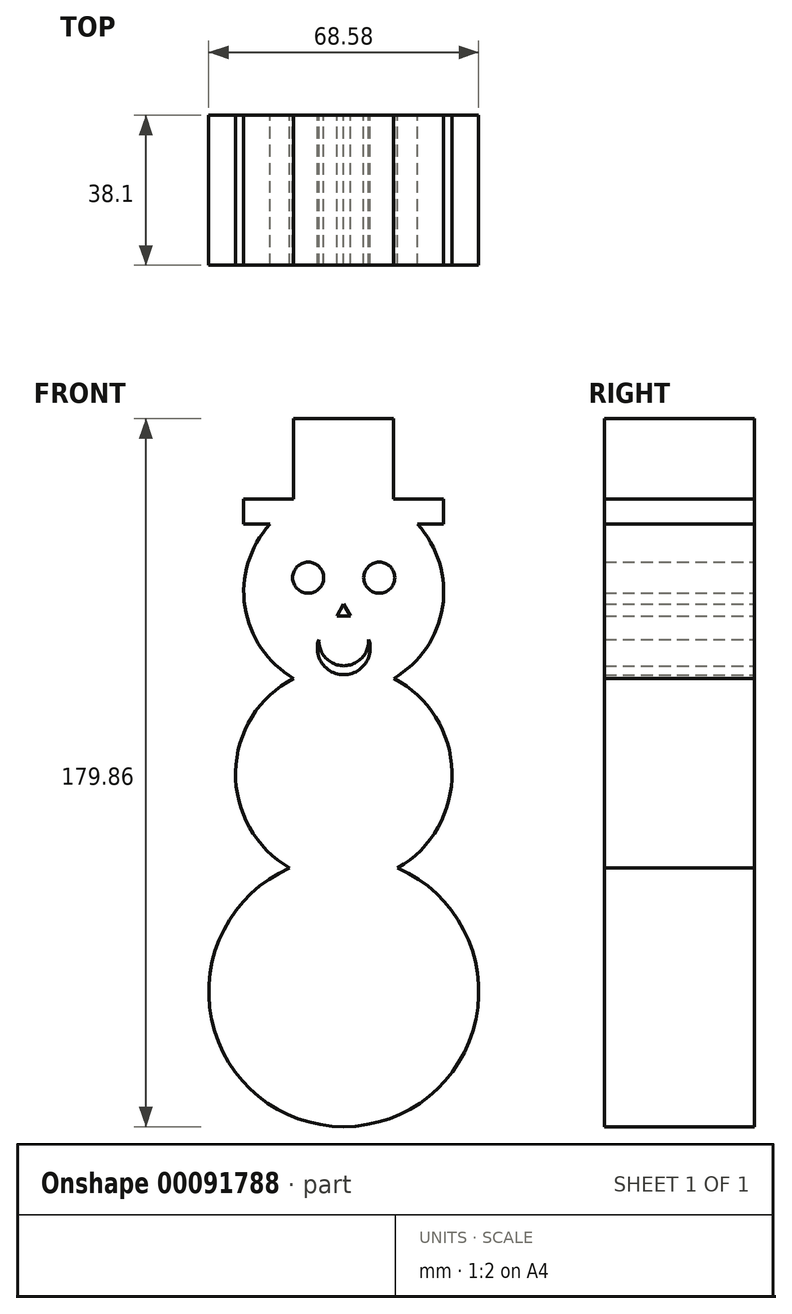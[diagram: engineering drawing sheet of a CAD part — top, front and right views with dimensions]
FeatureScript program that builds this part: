
annotation { "Feature Type Name" : "Feature", "Feature Type Description" : "" }
export const myFeature = defineFeature(function(context is Context, id is Id, definition is map)
    precondition{}
    {
        {
            var Q0;
            Q0=qCreatedBy(makeId("Front.planeOp"),FACE);
            var sketch = newSketch(context, id + "F0", { "sketchPlane" : qUnion([Q0])});
            skCircle(sketch, "E0", {"center": v(0, 0) * mm, "radius": 27.5 * mm});
            skCircle(sketch, "E1", {"center": v(0, 46.37) * mm, "radius": 25.4 * mm});
            skCircle(sketch, "E2", {"center": v(0, -55.26) * mm, "radius": 34.3 * mm});
            skCircle(sketch, "E3", {"center": v(-9.03, 49.92) * mm, "radius": 3.95 * mm});
            skCircle(sketch, "E4.MirrorC", {"center": v(9.03, 49.92) * mm, "radius": 3.95 * mm});
            skLineSegment(sketch, "E5", {"start": v(0, 43.2) * mm, "end": v(-1.7, 40.25) * mm});
            skLineSegment(sketch, "E6", {"start": v(-1.7, 40.25) * mm, "end": v(1.7, 40.25) * mm});
            skPoint(sketch, "E7.endSnap0", {"position": v(-0.85, 41.73) * mm});
            skLineSegment(sketch, "E8", {"start": v(0, 43.2) * mm, "end": v(1.7, 40.25) * mm});
            skArc(sketch, "E9", {"start": v(-6.34, 34.24) * mm, "mid": v(-4.6, 29.53) * mm, "end": v(0, 27.55) * mm});
            skArc(sketch, "E10", {"start": v(-6.34, 34.24) * mm, "mid": v(-5.5, 28.11) * mm, "end": v(0, 25.27) * mm});
            skArc(sketch, "E11.MirrorCS", {"start": v(6.34, 34.24) * mm, "mid": v(4.6, 29.53) * mm, "end": v(0, 27.55) * mm});
            skArc(sketch, "E12.MirrorCS", {"start": v(6.34, 34.24) * mm, "mid": v(5.5, 28.11) * mm, "end": v(0, 25.27) * mm});
            skSolve(sketch);
        }
        {
            var Q0;
            Q0 = qSketchRegion(id + "F0", true);
            extrude(context, id + "F1", {"entities" : qUnion([Q0]), "depth" : 38.1 * mm});
        }
        {
            var Q0;
            Q0=qCreatedBy(makeId("Front.planeOp"),FACE);
            var sketch = newSketch(context, id + "F2", { "sketchPlane" : qUnion([Q0])});
            skLineSegment(sketch, "E13.bottom", {"start": v(0, 69.85) * mm, "end": v(25.4, 69.85) * mm});
            skLineSegment(sketch, "E13.top", {"start": v(0, 63.5) * mm, "end": v(25.4, 63.5) * mm});
            skLineSegment(sketch, "E13.left", {"start": v(0, 69.85) * mm, "end": v(0, 63.5) * mm});
            skLineSegment(sketch, "E13.right", {"start": v(25.4, 69.85) * mm, "end": v(25.4, 63.5) * mm});
            skLineSegment(sketch, "E14.top", {"start": v(12.7, 90.3) * mm, "end": v(0, 90.3) * mm});
            skLineSegment(sketch, "E14.left", {"start": v(12.7, 69.85) * mm, "end": v(12.7, 90.3) * mm});
            skLineSegment(sketch, "E14.right", {"start": v(0, 69.85) * mm, "end": v(0, 90.3) * mm});
            skLineSegment(sketch, "E15.MirrorCS", {"start": v(-12.7, 90.3) * mm, "end": v(0, 90.3) * mm});
            skLineSegment(sketch, "E16.MirrorCS", {"start": v(-12.7, 69.85) * mm, "end": v(-12.7, 90.3) * mm});
            skLineSegment(sketch, "E17.MirrorCS", {"start": v(0, 63.5) * mm, "end": v(-25.4, 63.5) * mm});
            skLineSegment(sketch, "E18.MirrorCS", {"start": v(-25.4, 69.85) * mm, "end": v(-25.4, 63.5) * mm});
            skLineSegment(sketch, "E19.MirrorCS", {"start": v(0, 69.85) * mm, "end": v(-25.4, 69.85) * mm});
            skSolve(sketch);
        }
        {
            var Q0;
            Q0 = qSketchRegion(id + "F2", true);
            extrude(context, id + "F3", {"entities" : qUnion([Q0]), "depth" : 38.1 * mm});
        }
        {
            var Q0;
            Q0 = qSketchRegion(id + "F2", true);
            extrude(context, id + "F4", {"entities" : qUnion([Q0]), "operationType" : NewBodyOperationType.ADD, "depth" : 38.1 * mm});
        }
    });
